# Revit family: PlumFix_Tap_ABEY_Lucia_Wall Basin Set
name_source: partatom
category: Plumbing Fixtures
revit_build: Autodesk Revit 2015 (Build: 20140223_1515(x64)
units: mm (PartAtom-declared; Revit-internal decimal feet)

## types (2) — shared parameters
CW Connection = Yes
HW Connection = Yes
Manufacturer = Abey Australia
Manufacturer_Overall Depth = 220 mm  [stored 0.721785 ft]
Manufacturer_Overall Height = 118 mm
Manufacturer_Overall Width = 172 mm  [stored 0.564304 ft]
Manufacturer_URL__Product Specific = https://www.abey.com.au
URL = https://www.abey.com.au
Vent Connection = No
Waste Connection = No

## per-type parameters (varying)
| type | Description | Manufacturer_Spec Code | Model | PlumbingMaterial_ANZRS | Type Comments |
| Chrome | Lucia - Wall Basin Set - Chrome Finish | 3B-WS | 3B-WS | z_Abey_Chrome | Chrome Finish |
| Black | Lucia - Wall Basin Set - Black Finish | 3B-WS-B | 3B-WS-B | z_Abey_Black | Black Finish |

note: [stored X ft] marks values corroborated as IEEE doubles in the binary element streams (Revit-internal decimal feet)

## geometry (parser evidence)
native form markers: Sweep x2
no freeform markers — native parametric forms only
